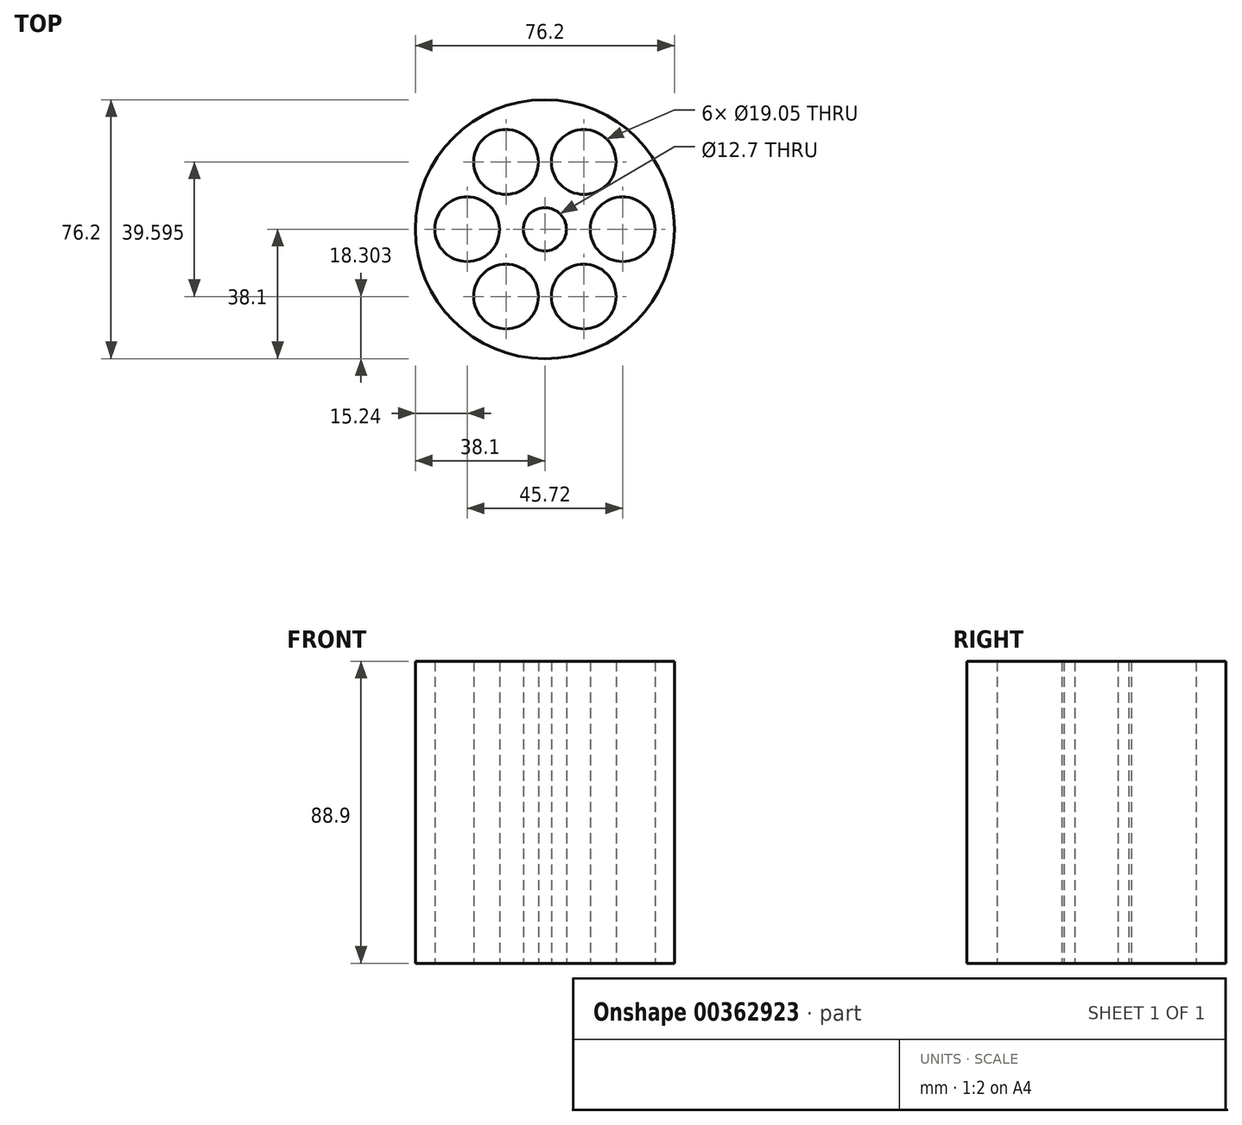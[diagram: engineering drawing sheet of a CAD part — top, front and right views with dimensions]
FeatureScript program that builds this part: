
annotation { "Feature Type Name" : "Feature", "Feature Type Description" : "" }
export const myFeature = defineFeature(function(context is Context, id is Id, definition is map)
    precondition{}
    {
        {
            var Q0;
            Q0=qCreatedBy(makeId("Top.planeOp"),FACE);
            var sketch = newSketch(context, id + "F0", { "sketchPlane" : qUnion([Q0])});
            skCircle(sketch, "E0", {"center": v(0, 0) * mm, "radius": 38.1 * mm});
            skSolve(sketch);
        }
        {
            var Q0;
            Q0 = qSketchRegion(id + "F0", true);
            extrude(context, id + "F1", {"entities" : qUnion([Q0]), "depth" : 88.9 * mm});
        }
        {
            var Q0;
            Q0=makeQuery(id+"F1.opExtrude","CAP_FACE",FACE,{"disambiguationData":[OSD([sQuery(id+"F0.wireOp",EDGE,"E0")])],"isStart":true});
            var sketch = newSketch(context, id + "F2", { "sketchPlane" : qUnion([Q0])});
            skPoint(sketch, "E1", {"position": v(0, 0) * mm});
            skPoint(sketch, "E2", {"position": v(-25.33, 0) * mm});
            skPoint(sketch, "E3.1.0", {"position": v(-12.67, -21.94) * mm});
            skPoint(sketch, "E3.2.0", {"position": v(12.67, -21.94) * mm});
            skPoint(sketch, "E3.3.0", {"position": v(25.33, 0) * mm});
            skPoint(sketch, "E3.4.0", {"position": v(12.67, 21.94) * mm});
            skPoint(sketch, "E3.5.0", {"position": v(-12.67, 21.94) * mm});
            skSolve(sketch);
        }
        {
            var Q0;
            Q0=sQuery(id+"F2.wireOp",VERTEX,"E1");
            var Q1;
            Q1=makeQuery(id+"F1.opExtrude","SWEPT_BODY",BODY,{"disambiguationData":[OSD([sQuery(id+"F0.wireOp",EDGE,"E0")])]});
            hole(context, id + "F3", {"style" : HoleStyle.SIMPLE, "endStyle" : HoleEndStyle.THROUGH, "holeDiameter" : 12.7 * mm, "isTappedThrough" : true, "tappedDepth" : 12.7 * mm, "tapClearance" : 3, "locations" : qUnion([Q0]), "scope" : qUnion([Q1])});
        }
        {
            var Q0;
            Q0=makeQuery(id+"F1.opExtrude","CAP_FACE",FACE,{"disambiguationData":[OSD([sQuery(id+"F0.wireOp",EDGE,"E0")])],"isStart":true});
            var sketch = newSketch(context, id + "F4", { "sketchPlane" : qUnion([Q0])});
            skPoint(sketch, "E4", {"position": v(-22.86, 0) * mm});
            skPoint(sketch, "E5.1.0", {"position": v(-11.43, -19.8) * mm});
            skPoint(sketch, "E5.2.0", {"position": v(11.43, -19.8) * mm});
            skPoint(sketch, "E5.3.0", {"position": v(22.86, 0) * mm});
            skPoint(sketch, "E5.4.0", {"position": v(11.43, 19.8) * mm});
            skPoint(sketch, "E5.5.0", {"position": v(-11.43, 19.8) * mm});
            skPoint(sketch, "E5.center", {"position": v(0, 0) * mm});
            skSolve(sketch);
        }
        {
            var Q0;
            Q0=sQuery(id+"F4.wireOp",VERTEX,"E4");
            var Q1;
            Q1=sQuery(id+"F4.wireOp",VERTEX,"E5.1.0");
            var Q2;
            Q2=sQuery(id+"F4.wireOp",VERTEX,"E5.2.0");
            var Q3;
            Q3=sQuery(id+"F4.wireOp",VERTEX,"E5.3.0");
            var Q4;
            Q4=sQuery(id+"F4.wireOp",VERTEX,"E5.4.0");
            var Q5;
            Q5=sQuery(id+"F4.wireOp",VERTEX,"E5.5.0");
            var Q6;
            Q6=makeQuery(id+"F1.opExtrude","SWEPT_BODY",BODY,{"disambiguationData":[OSD([sQuery(id+"F0.wireOp",EDGE,"E0")])]});
            hole(context, id + "F5", {"style" : HoleStyle.SIMPLE, "endStyle" : HoleEndStyle.THROUGH, "holeDiameter" : 19.05 * mm, "isTappedThrough" : true, "tappedDepth" : 12.7 * mm, "tapClearance" : 3, "locations" : qUnion([Q0, Q1, Q2, Q3, Q4, Q5]), "scope" : qUnion([Q6])});
        }
    });
